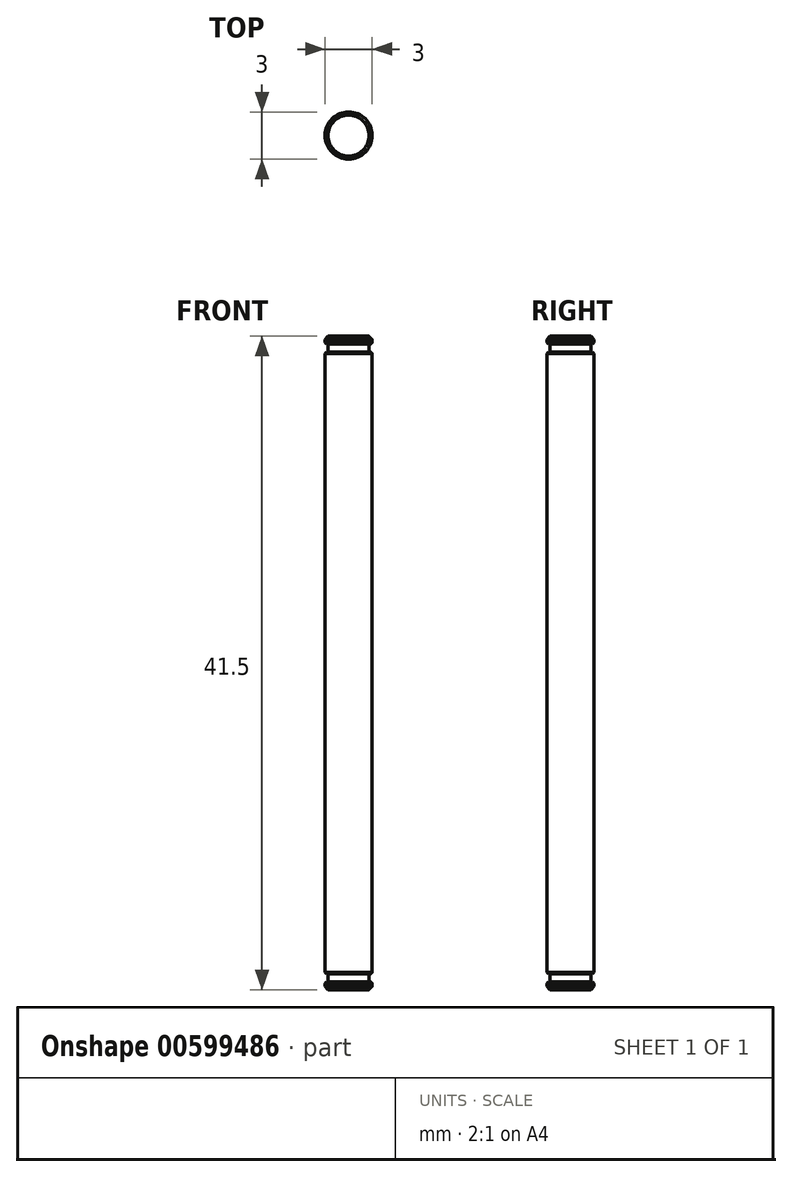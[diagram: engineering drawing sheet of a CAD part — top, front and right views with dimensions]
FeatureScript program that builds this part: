
annotation { "Feature Type Name" : "Feature", "Feature Type Description" : "" }
export const myFeature = defineFeature(function(context is Context, id is Id, definition is map)
    precondition{}
    {
        {
            var Q0;
            Q0=qCreatedBy(makeId("Top.planeOp"),FACE);
            var sketch = newSketch(context, id + "F0", { "sketchPlane" : qUnion([Q0])});
            skCircle(sketch, "E0", {"center": v(0, 0) * mm, "radius": 1.5 * mm});
            skCircle(sketch, "E1.0", {"center": v(0, 0) * mm, "radius": 1.3 * mm});
            skSolve(sketch);
        }
        {
            var Q0;
            Q0=qSketchRegion(id+"F0",true);
            var Q1;
            Q1=makeQuery(id+"F0.imprint","IMPRINT",FACE,{"disambiguationData":[TD([[makeQuery(id+"F0.imprint","IMPRINT",EDGE,{"derivedFrom":sQuery(id+"F0.wireOp",EDGE,"E1.0")}),1.0]])]});
            extrude(context, id + "F1", {"entities" : qUnion([Q0, Q1]), "depth" : 39.5 * mm, "offsetDistance" : 25 * mm});
        }
        {
            var Q0;
            Q0=makeQuery(id+"F0.imprint","IMPRINT",FACE,{"disambiguationData":[TD([[makeQuery(id+"F0.imprint","IMPRINT",EDGE,{"derivedFrom":sQuery(id+"F0.wireOp",EDGE,"E1.0")}),1.0]])]});
            extrude(context, id + "F2", {"entities" : qUnion([Q0]), "operationType" : NewBodyOperationType.ADD, "oppositeDirection" : true, "depth" : 1 * mm});
        }
        {
            var Q0;
            Q0=qSketchRegion(id+"F0",true);
            extrude(context, id + "F3", {"entities" : qUnion([Q0]), "operationType" : NewBodyOperationType.ADD, "oppositeDirection" : true, "depth" : 1 * mm, "hasSecondDirection" : true, "secondDirectionOppositeDirection" : true, "secondDirectionDepth" : 0.5 * mm});
        }
        {
            var Q0;
            Q0=makeQuery(id+"F1.opExtrude","CAP_FACE",FACE,{"disambiguationData":[OSD([sQuery(id+"F0.wireOp",EDGE,"E0")])],"isStart":false});
            var sketch = newSketch(context, id + "F4", { "sketchPlane" : qUnion([Q0])});
            skCircle(sketch, "E2.0", {"center": v(0, 0) * mm, "radius": 1.3 * mm});
            skSolve(sketch);
        }
        {
            var Q0;
            Q0=makeQuery(id+"F4.imprint","IMPRINT",FACE,{"disambiguationData":[TD([[makeQuery(id+"F4.imprint","IMPRINT",EDGE,{"derivedFrom":sQuery(id+"F4.wireOp",EDGE,"E2.0")}),1.0]])]});
            extrude(context, id + "F5", {"entities" : qUnion([Q0]), "operationType" : NewBodyOperationType.ADD, "depth" : 1 * mm, "offsetDistance" : 25 * mm});
        }
        {
            var Q0;
            Q0=makeQuery(id+"F1.opExtrude","CAP_FACE",FACE,{"disambiguationData":[OSD([sQuery(id+"F0.wireOp",EDGE,"E0")])],"isStart":false});
            extrude(context, id + "F6", {"entities" : qUnion([Q0]), "operationType" : NewBodyOperationType.ADD, "depth" : 1 * mm, "offsetDistance" : 25 * mm, "hasSecondDirection" : true, "secondDirectionOppositeDirection" : false, "secondDirectionDepth" : 0.5 * mm});
        }
        {
            var Q0;
            Q0=makeQuery(id+"F3.opExtrude","CAP_EDGE",EDGE,{"disambiguationData":[OSD([sQuery(id+"F0.wireOp",EDGE,"E0")])],"isStart":false});
            var Q1;
            Q1=makeQuery(id+"F6.opExtrude","CAP_EDGE",EDGE,{"disambiguationData":[OSD([sQuery(id+"F0.wireOp",EDGE,"E0")])],"isStart":false});
            chamfer(context, id + "F7", {"entities" : qUnion([Q0, Q1]), "width" : 0.2 * mm, "tangentPropagation" : true});
        }
        {
            var Q0;
            Q0=makeQuery(id+"F3.opExtrude","CAP_EDGE",EDGE,{"disambiguationData":[OSD([sQuery(id+"F0.wireOp",EDGE,"E0")])],"isStart":true});
            var Q1;
            Q1=makeQuery(id+"F1.opExtrude","CAP_EDGE",EDGE,{"disambiguationData":[OSD([sQuery(id+"F0.wireOp",EDGE,"E0")])],"isStart":true});
            var Q2;
            Q2=makeQuery(id+"F1.opExtrude","CAP_EDGE",EDGE,{"disambiguationData":[OSD([sQuery(id+"F0.wireOp",EDGE,"E0")])],"isStart":false});
            var Q3;
            Q3=makeQuery(id+"F6.opExtrude","CAP_EDGE",EDGE,{"disambiguationData":[OSD([sQuery(id+"F0.wireOp",EDGE,"E0")])],"isStart":true});
            chamfer(context, id + "F8", {"entities" : qUnion([Q0, Q1, Q2, Q3]), "width" : 0.1 * mm, "tangentPropagation" : true});
        }
    });
